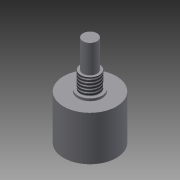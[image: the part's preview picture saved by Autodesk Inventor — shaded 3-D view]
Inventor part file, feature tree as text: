
AUTODESK INVENTOR PART (.ipt)
format: ipt  version: 2013 (Build 170138000, 138)  size: 94,720 bytes
history: native  units: mm
features: extrude x4, sketch x4, other x1, thread x1
ambient origin geometry x8: Origin, YZ Plane, XZ Plane, XY Plane, X Axis, Y Axis, Z Axis, Center Point
feature tree (10):
  other  "ソリッド1"
  extrude  "押し出し1"  Depth=22.5mm
  extrude  "押し出し2"  Depth=19.0mm TaperAngle=0.0deg
  extrude  "押し出し3"  Depth=10.3mm
  extrude  "押し出し4"  Depth=1.0mm TaperAngle=0.0deg
  thread  "ねじ1"
  sketch  "スケッチ1"
  sketch  "スケッチ2"
  sketch  "スケッチ3"
  sketch  "スケッチ4"
